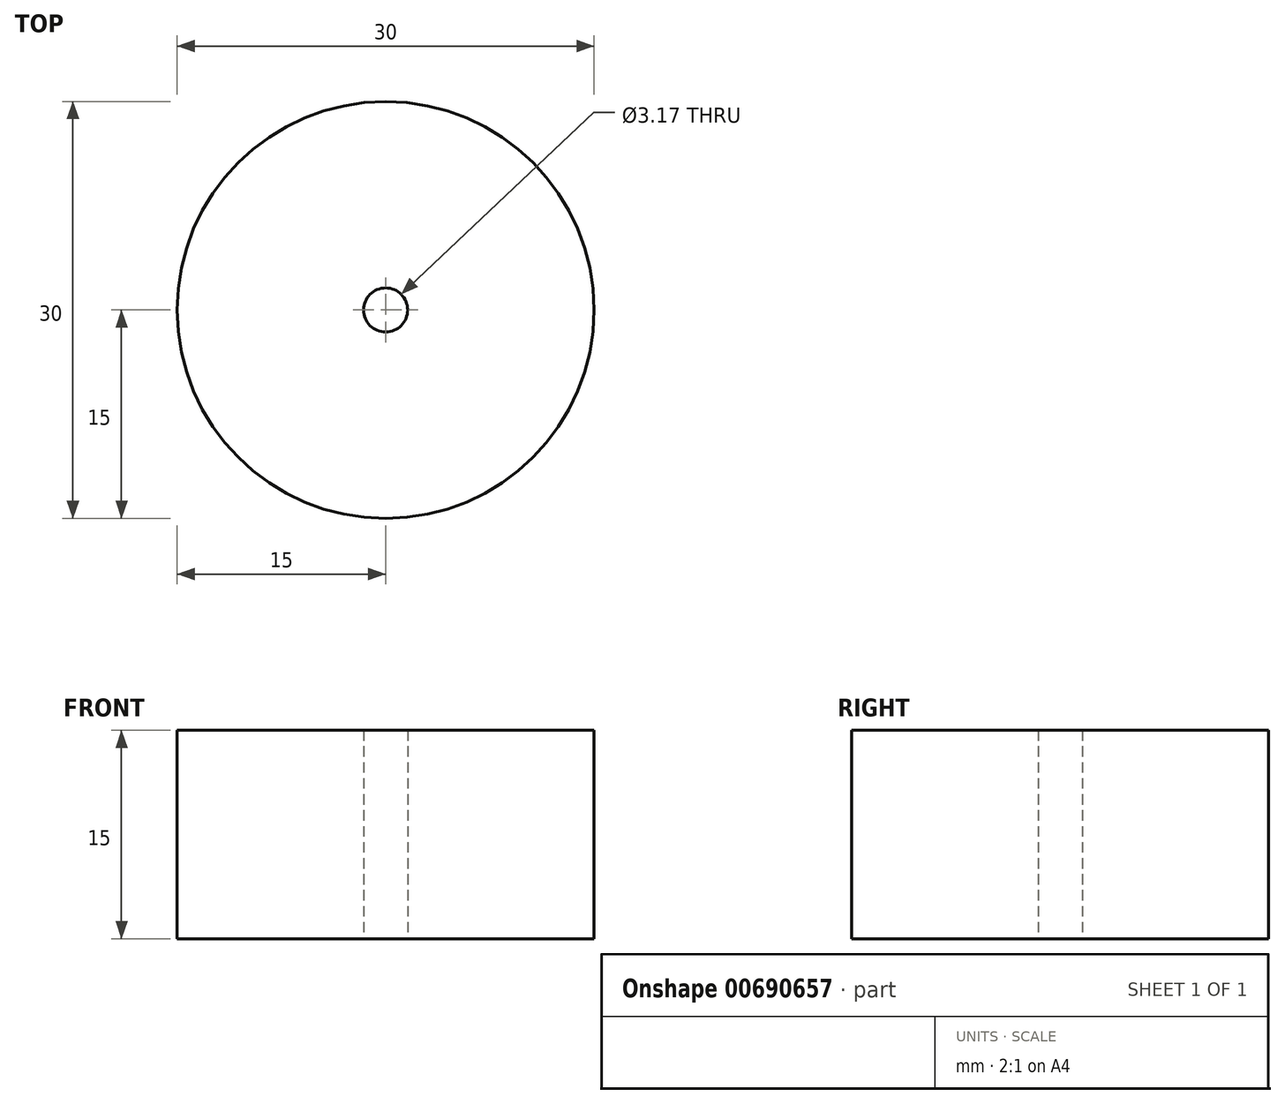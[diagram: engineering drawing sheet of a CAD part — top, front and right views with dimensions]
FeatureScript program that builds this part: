
annotation { "Feature Type Name" : "Feature", "Feature Type Description" : "" }
export const myFeature = defineFeature(function(context is Context, id is Id, definition is map)
    precondition{}
    {
        {
            var Q0;
            Q0=qCreatedBy(makeId("Top.planeOp"),FACE);
            var sketch = newSketch(context, id + "F0", { "sketchPlane" : qUnion([Q0])});
            skCircle(sketch, "E0", {"center": v(0, 0) * mm, "radius": 15 * mm});
            skCircle(sketch, "E1", {"center": v(0, 0) * mm, "radius": 1.59 * mm});
            skSolve(sketch);
        }
        {
            var Q0;
            Q0=makeQuery(id+"F0.imprint","IMPRINT",FACE,{"disambiguationData":[TD([[makeQuery(id+"F0.imprint","IMPRINT",EDGE,{"derivedFrom":sQuery(id+"F0.wireOp",EDGE,"E0")}),1.0]])]});
            extrude(context, id + "F1", {"entities" : qUnion([Q0]), "depth" : 15 * mm, "offsetDistance" : 25 * mm});
        }
    });
